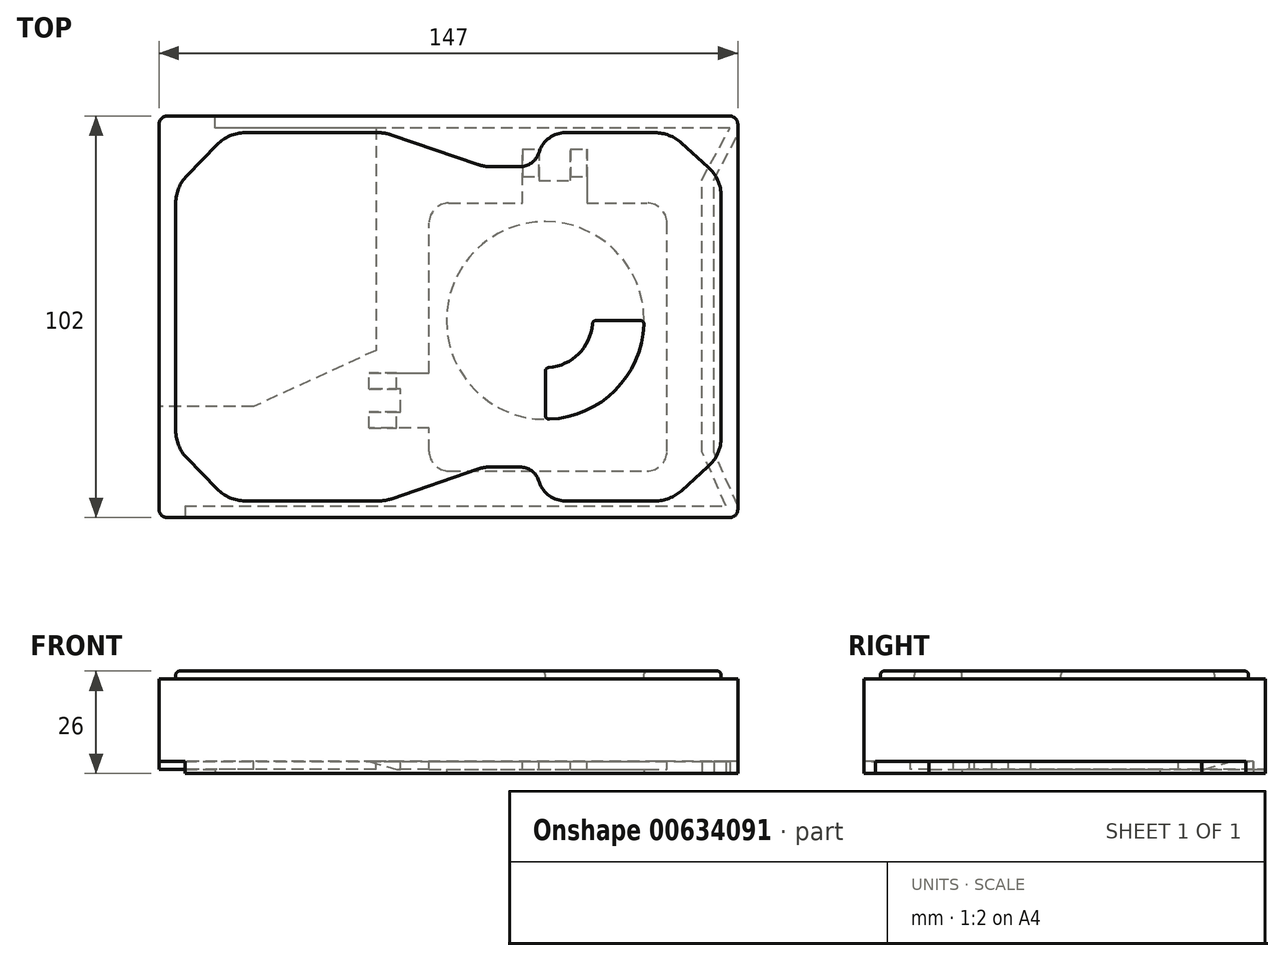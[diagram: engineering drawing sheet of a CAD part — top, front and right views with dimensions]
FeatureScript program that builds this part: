
annotation { "Feature Type Name" : "Feature", "Feature Type Description" : "" }
export const myFeature = defineFeature(function(context is Context, id is Id, definition is map)
    precondition{}
    {
        {
            var Q0;
            Q0=qCreatedBy(makeId("Top.planeOp"),FACE);
            var sketch = newSketch(context, id + "F0", { "sketchPlane" : qUnion([Q0])});
            skLineSegment(sketch, "E0.bottom", {"start": v(0, 0) * mm, "end": v(147, 0) * mm});
            skLineSegment(sketch, "E0.top", {"start": v(0, 102) * mm, "end": v(147, 102) * mm});
            skLineSegment(sketch, "E0.left", {"start": v(0, 0) * mm, "end": v(0, 102) * mm});
            skLineSegment(sketch, "E0.right", {"start": v(147, 0) * mm, "end": v(147, 102) * mm});
            skSolve(sketch);
        }
        {
            var Q0;
            Q0=makeQuery(id+"F0.imprint","IMPRINT",FACE,{"disambiguationData":[TD([[makeQuery(id+"F0.imprint","IMPRINT",EDGE,{"derivedFrom":sQuery(id+"F0.wireOp",EDGE,"E0.bottom")}),1.0]])]});
            extrude(context, id + "F1", {"entities" : qUnion([Q0]), "depth" : 26 * mm, "offsetDistance" : 25 * mm});
        }
        {
            var Q0;
            Q0=makeQuery(id+"F1.opExtrude","SWEPT_EDGE",EDGE,{"disambiguationData":[OSD([sQuery(id+"F0.wireOp",EDGE,"E0.bottom"),sQuery(id+"F0.wireOp",EDGE,"E0.left")])]});
            var Q1;
            Q1=makeQuery(id+"F1.opExtrude","SWEPT_EDGE",EDGE,{"disambiguationData":[OSD([sQuery(id+"F0.wireOp",EDGE,"E0.bottom"),sQuery(id+"F0.wireOp",EDGE,"E0.right")])]});
            var Q2;
            Q2=makeQuery(id+"F1.opExtrude","SWEPT_EDGE",EDGE,{"disambiguationData":[OSD([sQuery(id+"F0.wireOp",EDGE,"E0.top"),sQuery(id+"F0.wireOp",EDGE,"E0.right")])]});
            var Q3;
            Q3=makeQuery(id+"F1.opExtrude","SWEPT_EDGE",EDGE,{"disambiguationData":[OSD([sQuery(id+"F0.wireOp",EDGE,"E0.top"),sQuery(id+"F0.wireOp",EDGE,"E0.left")])]});
            fillet(context, id + "F2", {"entities" : qUnion([Q0, Q1, Q2, Q3]), "radius" : 2 * mm, "tangentPropagation" : true, "allowEdgeOverflow" : false});
        }
        {
            var Q0;
            Q0=makeQuery(id+"F1.opExtrude","CAP_FACE",FACE,{"disambiguationData":[OSD([sQuery(id+"F0.wireOp",EDGE,"E0.bottom"),sQuery(id+"F0.wireOp",EDGE,"E0.top"),sQuery(id+"F0.wireOp",EDGE,"E0.left"),sQuery(id+"F0.wireOp",EDGE,"E0.right")])],"isStart":true});
            var sketch = newSketch(context, id + "F3", { "sketchPlane" : qUnion([Q0])});
            skLineSegment(sketch, "E1", {"start": v(6.56, -3) * mm, "end": v(144, -3) * mm});
            skLineSegment(sketch, "E2", {"start": v(144, -3) * mm, "end": v(137.95, -16.63) * mm});
            skLineSegment(sketch, "E3", {"start": v(137.95, -16.63) * mm, "end": v(137.95, -85.86) * mm});
            skLineSegment(sketch, "E4", {"start": v(137.95, -85.86) * mm, "end": v(145, -99) * mm});
            skLineSegment(sketch, "E5", {"start": v(145, -99) * mm, "end": v(14.23, -99) * mm});
            skLineSegment(sketch, "E6", {"start": v(6.56, -3) * mm, "end": v(6.56, 0) * mm});
            skLineSegment(sketch, "E7", {"start": v(147, -3) * mm, "end": v(140.95, -16.63) * mm});
            skLineSegment(sketch, "E8", {"start": v(140.95, -16.63) * mm, "end": v(140.95, -85.86) * mm});
            skLineSegment(sketch, "E9", {"start": v(140.95, -85.86) * mm, "end": v(147, -97.14) * mm});
            skLineSegment(sketch, "E10", {"start": v(14.23, -99) * mm, "end": v(14.23, -102) * mm});
            skLineSegment(sketch, "E11", {"start": v(140.95, -16.63) * mm, "end": v(137.95, -16.63) * mm, "construction": true});
            skLineSegment(sketch, "E12", {"start": v(145, -99) * mm, "end": v(147, -99) * mm, "construction": true});
            skLineSegment(sketch, "E13", {"start": v(144, -3) * mm, "end": v(147, -3) * mm, "construction": true});
            skLineSegment(sketch, "E14", {"start": v(137.95, -85.86) * mm, "end": v(140.95, -85.86) * mm, "construction": true});
            skCircle(sketch, "E15", {"center": v(98.1, -50.09) * mm, "radius": 25.12 * mm});
            skSolve(sketch);
        }
        {
            var Q0;
            Q0=makeQuery(id+"F3.imprint","IMPRINT",FACE,{"disambiguationData":[TD([[makeQuery(id+"F3.imprint","IMPRINT",EDGE,{"derivedFrom":sQuery(id+"F3.wireOp",EDGE,"E1")}),-1.0]])]});
            var Q1;
            Q1=makeQuery(id+"F3.imprint","IMPRINT",FACE,{"disambiguationData":[TD([[makeQuery(id+"F3.imprint","IMPRINT",EDGE,{"derivedFrom":sQuery(id+"F3.wireOp",EDGE,"E7")}),1.0]])]});
            extrude(context, id + "F4", {"entities" : qUnion([Q0, Q1]), "operationType" : NewBodyOperationType.REMOVE, "oppositeDirection" : true, "depth" : 3 * mm, "offsetDistance" : 25 * mm});
        }
        {
            var Q0;
            Q0=makeQuery(id+"F4.boolean.opBoolean","COPY",FACE,{"derivedFrom":makeQuery(id+"F4.opExtrude","CAP_FACE",FACE,{"disambiguationData":[OSD([sQuery(id+"F0.wireOp",EDGE,"E0.bottom"),sQuery(id+"F0.wireOp",EDGE,"E0.top"),sQuery(id+"F0.wireOp",EDGE,"E0.left"),sQuery(id+"F0.wireOp",EDGE,"E0.right"),sQuery(id+"F3.wireOp",EDGE,"E1"),sQuery(id+"F3.wireOp",EDGE,"E2"),sQuery(id+"F3.wireOp",EDGE,"E3"),sQuery(id+"F3.wireOp",EDGE,"E4"),sQuery(id+"F3.wireOp",EDGE,"E5"),sQuery(id+"F3.wireOp",EDGE,"E6"),sQuery(id+"F3.wireOp",EDGE,"E10"),sQuery(id+"F3.wireOp",EDGE,"E15")])],"isStart":false})});
            var sketch = newSketch(context, id + "F5", { "sketchPlane" : qUnion([Q0])});
            skLineSegment(sketch, "E16", {"start": v(55.07, -99) * mm, "end": v(55.07, -42.5) * mm});
            skLineSegment(sketch, "E17", {"start": v(55.07, -42.5) * mm, "end": v(23.96, -28.17) * mm});
            skLineSegment(sketch, "E18", {"start": v(23.96, -28.17) * mm, "end": v(0, -28.17) * mm});
            skSolve(sketch);
        }
        {
            var Q0;
            {var subQ3=sQuery(id+"F5.wireOp",EDGE,"E16");Q0=makeQuery(id+"F5.imprint","IMPRINT",FACE,{"disambiguationData":[TD([[makeQuery(id+"F5.imprint","IMPRINT",EDGE,{"derivedFrom":subQ3}),1.0]])]});}
            extrude(context, id + "F6", {"entities" : qUnion([Q0]), "operationType" : NewBodyOperationType.ADD, "depth" : 2 * mm, "offsetDistance" : 25 * mm});
        }
        {
            var Q0;
            Q0=makeQuery(id+"F4.boolean.opBoolean","COPY",FACE,{"derivedFrom":makeQuery(id+"F4.opExtrude","CAP_FACE",FACE,{"disambiguationData":[OSD([sQuery(id+"F0.wireOp",EDGE,"E0.bottom"),sQuery(id+"F0.wireOp",EDGE,"E0.top"),sQuery(id+"F0.wireOp",EDGE,"E0.left"),sQuery(id+"F0.wireOp",EDGE,"E0.right"),sQuery(id+"F3.wireOp",EDGE,"E1"),sQuery(id+"F3.wireOp",EDGE,"E2"),sQuery(id+"F3.wireOp",EDGE,"E3"),sQuery(id+"F3.wireOp",EDGE,"E4"),sQuery(id+"F3.wireOp",EDGE,"E5"),sQuery(id+"F3.wireOp",EDGE,"E6"),sQuery(id+"F3.wireOp",EDGE,"E10"),sQuery(id+"F3.wireOp",EDGE,"E15")])],"isStart":false})});
            var sketch = newSketch(context, id + "F7", { "sketchPlane" : qUnion([Q0])});
            skLineSegment(sketch, "E19", {"start": v(68.58, -22.73) * mm, "end": v(53.34, -22.73) * mm});
            skLineSegment(sketch, "E20", {"start": v(53.34, -22.73) * mm, "end": v(53.34, -26.85) * mm});
            skLineSegment(sketch, "E21", {"start": v(53.34, -26.85) * mm, "end": v(61.31, -26.85) * mm});
            skLineSegment(sketch, "E22", {"start": v(61.31, -26.85) * mm, "end": v(61.31, -32.61) * mm});
            skLineSegment(sketch, "E23", {"start": v(61.31, -32.61) * mm, "end": v(53.34, -32.61) * mm});
            skLineSegment(sketch, "E24", {"start": v(53.34, -32.61) * mm, "end": v(53.34, -36.74) * mm});
            skLineSegment(sketch, "E25", {"start": v(53.34, -36.74) * mm, "end": v(68.58, -36.74) * mm});
            skLineSegment(sketch, "E26", {"start": v(92.32, -79.88) * mm, "end": v(92.32, -93.65) * mm});
            skLineSegment(sketch, "E27", {"start": v(92.32, -93.65) * mm, "end": v(96.45, -93.65) * mm});
            skLineSegment(sketch, "E28", {"start": v(96.45, -93.65) * mm, "end": v(96.45, -85.67) * mm});
            skLineSegment(sketch, "E29", {"start": v(96.45, -85.67) * mm, "end": v(104.52, -85.67) * mm});
            skLineSegment(sketch, "E30", {"start": v(104.52, -85.67) * mm, "end": v(104.52, -93.65) * mm});
            skLineSegment(sketch, "E31", {"start": v(104.52, -93.65) * mm, "end": v(108.64, -93.65) * mm});
            skLineSegment(sketch, "E32", {"start": v(108.64, -93.65) * mm, "end": v(108.64, -79.88) * mm});
            skLineSegment(sketch, "E33.bottom", {"start": v(68.58, -11.84) * mm, "end": v(129, -11.84) * mm});
            skLineSegment(sketch, "E33.top", {"start": v(68.58, -79.88) * mm, "end": v(129, -79.88) * mm});
            skLineSegment(sketch, "E33.left", {"start": v(68.58, -11.84) * mm, "end": v(68.58, -79.88) * mm});
            skLineSegment(sketch, "E33.right", {"start": v(129, -11.84) * mm, "end": v(129, -79.88) * mm});
            skLineSegment(sketch, "E34", {"start": v(61.31, -26.85) * mm, "end": v(61.31, -22.73) * mm});
            skLineSegment(sketch, "E35", {"start": v(61.31, -32.61) * mm, "end": v(61.31, -36.74) * mm});
            skLineSegment(sketch, "E36", {"start": v(96.45, -85.67) * mm, "end": v(92.32, -85.67) * mm});
            skLineSegment(sketch, "E37", {"start": v(104.52, -85.67) * mm, "end": v(108.64, -85.67) * mm});
            skSolve(sketch);
        }
        {
            var Q0;
            {var subQ6=sQuery(id+"F7.wireOp",EDGE,"E33.bottom");Q0=makeQuery(id+"F7.imprint","IMPRINT",FACE,{"disambiguationData":[TD([[makeQuery(id+"F7.imprint","IMPRINT",EDGE,{"derivedFrom":subQ6}),-1.0]])]});}
            var Q1;
            Q1=makeQuery(id+"F7.imprint","IMPRINT",FACE,{"disambiguationData":[TD([[makeQuery(id+"F7.imprint","IMPRINT",EDGE,{"derivedFrom":sQuery(id+"F7.wireOp",EDGE,"E22")}),1.0]])]});
            var Q2;
            Q2=makeQuery(id+"F7.imprint","IMPRINT",FACE,{"disambiguationData":[TD([[makeQuery(id+"F7.imprint","IMPRINT",EDGE,{"derivedFrom":sQuery(id+"F7.wireOp",EDGE,"E29")}),1.0]])]});
            var Q3;
            {var subQ0=sQuery(id+"F7.wireOp",EDGE,"E20");Q3=makeQuery(id+"F7.imprint","IMPRINT",FACE,{"disambiguationData":[TD([[makeQuery(id+"F7.imprint","IMPRINT",EDGE,{"derivedFrom":subQ0}),1.0]])]});}
            var Q4;
            Q4=makeQuery(id+"F7.imprint","IMPRINT",FACE,{"disambiguationData":[TD([[makeQuery(id+"F7.imprint","IMPRINT",EDGE,{"derivedFrom":sQuery(id+"F7.wireOp",EDGE,"E23")}),1.0]])]});
            var Q5;
            {var subQ0=sQuery(id+"F7.wireOp",EDGE,"E27");Q5=makeQuery(id+"F7.imprint","IMPRINT",FACE,{"disambiguationData":[TD([[makeQuery(id+"F7.imprint","IMPRINT",EDGE,{"derivedFrom":subQ0}),1.0]])]});}
            var Q6;
            Q6=makeQuery(id+"F7.imprint","IMPRINT",FACE,{"disambiguationData":[TD([[makeQuery(id+"F7.imprint","IMPRINT",EDGE,{"derivedFrom":sQuery(id+"F7.wireOp",EDGE,"E30")}),1.0]])]});
            extrude(context, id + "F8", {"entities" : qUnion([Q0, Q1, Q2, Q3, Q4, Q5, Q6]), "operationType" : NewBodyOperationType.ADD, "depth" : 2 * mm, "offsetDistance" : 25 * mm});
        }
        {
            var Q0;
            Q0=makeQuery(id+"F8.opExtrude","CAP_EDGE",EDGE,{"disambiguationData":[OSD([sQuery(id+"F7.wireOp",EDGE,"E20")])],"isStart":false});
            var Q1;
            Q1=makeQuery(id+"F8.opExtrude","CAP_EDGE",EDGE,{"disambiguationData":[OSD([sQuery(id+"F7.wireOp",EDGE,"E24")])],"isStart":false});
            var Q2;
            Q2=makeQuery(id+"F8.opExtrude","CAP_EDGE",EDGE,{"disambiguationData":[OSD([sQuery(id+"F7.wireOp",EDGE,"E27")])],"isStart":false});
            var Q3;
            Q3=makeQuery(id+"F8.opExtrude","CAP_EDGE",EDGE,{"disambiguationData":[OSD([sQuery(id+"F7.wireOp",EDGE,"E31")])],"isStart":false});
            chamfer(context, id + "F9", {"entities" : qUnion([Q0, Q1, Q2, Q3]), "chamferType" : ChamferType.TWO_OFFSETS, "width1" : 7 * mm, "oppositeDirection" : false, "width2" : 2 * mm, "tangentPropagation" : true});
        }
        {
            var Q0;
            Q0=makeQuery(id+"F8.opExtrude","SWEPT_EDGE",EDGE,{"disambiguationData":[OSD([sQuery(id+"F7.wireOp",EDGE,"E33.bottom"),sQuery(id+"F7.wireOp",EDGE,"E33.left")])]});
            var Q1;
            Q1=makeQuery(id+"F8.opExtrude","SWEPT_EDGE",EDGE,{"disambiguationData":[OSD([sQuery(id+"F7.wireOp",EDGE,"E33.bottom"),sQuery(id+"F7.wireOp",EDGE,"E33.right")])]});
            var Q2;
            Q2=makeQuery(id+"F8.opExtrude","SWEPT_EDGE",EDGE,{"disambiguationData":[OSD([sQuery(id+"F7.wireOp",EDGE,"E33.top"),sQuery(id+"F7.wireOp",EDGE,"E33.right")])]});
            var Q3;
            Q3=makeQuery(id+"F8.opExtrude","SWEPT_EDGE",EDGE,{"disambiguationData":[OSD([sQuery(id+"F7.wireOp",EDGE,"E33.top"),sQuery(id+"F7.wireOp",EDGE,"E33.left")])]});
            fillet(context, id + "F10", {"entities" : qUnion([Q0, Q1, Q2, Q3]), "radius" : 5 * mm, "tangentPropagation" : true, "allowEdgeOverflow" : false});
        }
        {
            var Q0;
            Q0=makeQuery(id+"F1.opExtrude","CAP_FACE",FACE,{"disambiguationData":[OSD([sQuery(id+"F0.wireOp",EDGE,"E0.bottom"),sQuery(id+"F0.wireOp",EDGE,"E0.top"),sQuery(id+"F0.wireOp",EDGE,"E0.left"),sQuery(id+"F0.wireOp",EDGE,"E0.right")])],"isStart":false});
            var sketch = newSketch(context, id + "F11", { "sketchPlane" : qUnion([Q0])});
            skLineSegment(sketch, "E38", {"start": v(4.23, 51) * mm, "end": v(4.23, 22.07) * mm});
            skLineSegment(sketch, "E39", {"start": v(7.06, 15.1) * mm, "end": v(14.7, 7.25) * mm});
            skLineSegment(sketch, "E40", {"start": v(21.86, 4.23) * mm, "end": v(55.75, 4.23) * mm});
            skLineSegment(sketch, "E41", {"start": v(59, 4.77) * mm, "end": v(80.96, 12.3) * mm});
            skLineSegment(sketch, "E42", {"start": v(84.2, 12.84) * mm, "end": v(91.68, 12.84) * mm});
            skLineSegment(sketch, "E43", {"start": v(96.41, 9.47) * mm, "end": v(96.59, 8.95) * mm});
            skLineSegment(sketch, "E44", {"start": v(103.21, 4.23) * mm, "end": v(125.96, 4.23) * mm});
            skLineSegment(sketch, "E45", {"start": v(132.66, 6.8) * mm, "end": v(139.47, 12.94) * mm});
            skLineSegment(sketch, "E46", {"start": v(142.77, 20.37) * mm, "end": v(142.77, 51) * mm});
            skLineSegment(sketch, "E47", {"start": v(147, 51) * mm, "end": v(0, 51) * mm, "construction": true});
            skLineSegment(sketch, "E48", {"start": v(4.23, 51) * mm, "end": v(0, 51) * mm, "construction": true});
            skLineSegment(sketch, "E49", {"start": v(142.77, 51) * mm, "end": v(147, 51) * mm, "construction": true});
            skLineSegment(sketch, "E50", {"start": v(129.8, 4.23) * mm, "end": v(129.8, 0) * mm, "construction": true});
            skPoint(sketch, "E51.visualSharp", {"position": v(142.77, 15.92) * mm});
            skArc(sketch, "E51.filletArc", {"start": v(139.47, 12.94) * mm, "mid": v(141.91, 16.3) * mm, "end": v(142.77, 20.37) * mm});
            skPoint(sketch, "E52.visualSharp", {"position": v(129.8, 4.23) * mm});
            skArc(sketch, "E52.filletArc", {"start": v(125.96, 4.23) * mm, "mid": v(129.55, 4.9) * mm, "end": v(132.66, 6.8) * mm});
            skPoint(sketch, "E53.visualSharp", {"position": v(98.21, 4.23) * mm});
            skArc(sketch, "E53.filletArc", {"start": v(96.59, 8.95) * mm, "mid": v(99.14, 5.53) * mm, "end": v(103.21, 4.23) * mm});
            skPoint(sketch, "E54.visualSharp", {"position": v(82.54, 12.84) * mm});
            skArc(sketch, "E54.filletArc", {"start": v(84.2, 12.84) * mm, "mid": v(82.56, 12.7) * mm, "end": v(80.96, 12.3) * mm});
            skPoint(sketch, "E55.visualSharp", {"position": v(57.42, 4.23) * mm});
            skArc(sketch, "E55.filletArc", {"start": v(55.75, 4.23) * mm, "mid": v(57.4, 4.36) * mm, "end": v(59, 4.77) * mm});
            skPoint(sketch, "E56.visualSharp", {"position": v(17.64, 4.23) * mm});
            skArc(sketch, "E56.filletArc", {"start": v(14.7, 7.25) * mm, "mid": v(17.97, 5.01) * mm, "end": v(21.86, 4.23) * mm});
            skPoint(sketch, "E57.visualSharp", {"position": v(4.23, 18) * mm});
            skArc(sketch, "E57.filletArc", {"start": v(4.23, 22.07) * mm, "mid": v(4.96, 18.3) * mm, "end": v(7.06, 15.1) * mm});
            skPoint(sketch, "E58.visualSharp", {"position": v(95.25, 12.84) * mm});
            skArc(sketch, "E58.filletArc", {"start": v(96.41, 9.47) * mm, "mid": v(94.59, 11.91) * mm, "end": v(91.68, 12.84) * mm});
            skLineSegment(sketch, "E59.MirrorCS", {"start": v(96.41, 92.53) * mm, "end": v(96.59, 93.05) * mm});
            skArc(sketch, "E60.MirrorCS", {"start": v(125.96, 97.77) * mm, "mid": v(129.55, 97.1) * mm, "end": v(132.66, 95.2) * mm});
            skArc(sketch, "E61.MirrorCS", {"start": v(84.2, 89.16) * mm, "mid": v(82.56, 89.3) * mm, "end": v(80.96, 89.7) * mm});
            skArc(sketch, "E62.MirrorCS", {"start": v(55.75, 97.77) * mm, "mid": v(57.4, 97.64) * mm, "end": v(59, 97.23) * mm});
            skArc(sketch, "E63.MirrorCS", {"start": v(14.7, 94.75) * mm, "mid": v(17.97, 96.99) * mm, "end": v(21.86, 97.77) * mm});
            skArc(sketch, "E64.MirrorCS", {"start": v(96.41, 92.53) * mm, "mid": v(94.59, 90.09) * mm, "end": v(91.68, 89.16) * mm});
            skArc(sketch, "E65.MirrorCS", {"start": v(4.23, 79.93) * mm, "mid": v(4.96, 83.7) * mm, "end": v(7.06, 86.9) * mm});
            skArc(sketch, "E66.MirrorCS", {"start": v(96.59, 93.05) * mm, "mid": v(99.14, 96.47) * mm, "end": v(103.21, 97.77) * mm});
            skArc(sketch, "E67.MirrorCS", {"start": v(139.47, 89.06) * mm, "mid": v(141.91, 85.7) * mm, "end": v(142.77, 81.63) * mm});
            skPoint(sketch, "E68.MirrorP", {"position": v(4.23, 84) * mm});
            skPoint(sketch, "E69.MirrorP", {"position": v(129.8, 97.77) * mm});
            skLineSegment(sketch, "E70.MirrorCS", {"start": v(4.23, 51) * mm, "end": v(4.23, 79.93) * mm});
            skLineSegment(sketch, "E71.MirrorCS", {"start": v(103.21, 97.77) * mm, "end": v(125.96, 97.77) * mm});
            skPoint(sketch, "E72.MirrorP", {"position": v(98.21, 97.77) * mm});
            skLineSegment(sketch, "E73.MirrorCS", {"start": v(132.66, 95.2) * mm, "end": v(139.47, 89.06) * mm});
            skLineSegment(sketch, "E74.MirrorCS", {"start": v(21.86, 97.77) * mm, "end": v(55.75, 97.77) * mm});
            skPoint(sketch, "E75.MirrorP", {"position": v(17.64, 97.77) * mm});
            skLineSegment(sketch, "E76.MirrorCS", {"start": v(7.06, 86.9) * mm, "end": v(14.7, 94.75) * mm});
            skLineSegment(sketch, "E77.MirrorCS", {"start": v(59, 97.23) * mm, "end": v(80.96, 89.7) * mm});
            skPoint(sketch, "E78.MirrorP", {"position": v(82.54, 89.16) * mm});
            skPoint(sketch, "E79.MirrorP", {"position": v(142.77, 86.08) * mm});
            skPoint(sketch, "E80.MirrorP", {"position": v(95.25, 89.16) * mm});
            skPoint(sketch, "E81.MirrorP", {"position": v(57.42, 97.77) * mm});
            skLineSegment(sketch, "E82.MirrorCS", {"start": v(84.2, 89.16) * mm, "end": v(91.68, 89.16) * mm});
            skLineSegment(sketch, "E83.MirrorCS", {"start": v(142.77, 81.63) * mm, "end": v(142.77, 51) * mm});
            skLineSegment(sketch, "E84", {"start": v(98.1, 37.13) * mm, "end": v(98.1, 26) * mm});
            skLineSegment(sketch, "E85", {"start": v(122.2, 50.09) * mm, "end": v(111.06, 50.09) * mm});
            skLineSegment(sketch, "E86", {"start": v(110.1, 50.09) * mm, "end": v(98.1, 50.09) * mm, "construction": true});
            skLineSegment(sketch, "E87", {"start": v(98.1, 50.09) * mm, "end": v(98.1, 38.09) * mm, "construction": true});
            skArc(sketch, "E88", {"start": v(99.02, 38.12) * mm, "mid": v(106.58, 41.6) * mm, "end": v(110.06, 49.16) * mm});
            skArc(sketch, "E89", {"start": v(99.14, 25) * mm, "mid": v(115.86, 32.33) * mm, "end": v(123.2, 49.05) * mm});
            skPoint(sketch, "E90.visualSharp", {"position": v(123.22, 50.09) * mm});
            skArc(sketch, "E90.filletArc", {"start": v(123.2, 49.05) * mm, "mid": v(122.92, 49.78) * mm, "end": v(122.2, 50.09) * mm});
            skPoint(sketch, "E91.visualSharp", {"position": v(98.1, 24.97) * mm});
            skArc(sketch, "E91.filletArc", {"start": v(98.1, 26) * mm, "mid": v(98.4, 25.27) * mm, "end": v(99.14, 25) * mm});
            skPoint(sketch, "E92.visualSharp", {"position": v(98.1, 38.09) * mm});
            skArc(sketch, "E92.filletArc", {"start": v(99.02, 38.12) * mm, "mid": v(98.37, 37.8) * mm, "end": v(98.1, 37.13) * mm});
            skPoint(sketch, "E93.visualSharp", {"position": v(110.1, 50.09) * mm});
            skArc(sketch, "E93.filletArc", {"start": v(111.06, 50.09) * mm, "mid": v(110.38, 49.82) * mm, "end": v(110.06, 49.16) * mm});
            skCircle(sketch, "E94.0", {"center": v(98.1, 50.09) * mm, "radius": 25.12 * mm, "construction": true});
            skSolve(sketch);
        }
        {
            var Q0;
            Q0=makeQuery(id+"F11.imprint","IMPRINT",FACE,{"disambiguationData":[TD([[makeQuery(id+"F11.imprint","IMPRINT",EDGE,{"derivedFrom":sQuery(id+"F11.wireOp",EDGE,"E38")}),-1.0]])]});
            var Q1;
            Q1=makeQuery(id+"F11.imprint","IMPRINT",FACE,{"disambiguationData":[TD([[makeQuery(id+"F11.imprint","IMPRINT",EDGE,{"derivedFrom":sQuery(id+"F11.wireOp",EDGE,"E84")}),1.0]])]});
            extrude(context, id + "F12", {"entities" : qUnion([Q0, Q1]), "operationType" : NewBodyOperationType.REMOVE, "oppositeDirection" : true, "depth" : 2 * mm, "offsetDistance" : 25 * mm});
        }
        {
            var Q0;
            Q0=makeQuery(id+"F1.opExtrude","CAP_FACE",FACE,{"disambiguationData":[OSD([sQuery(id+"F0.wireOp",EDGE,"E0.bottom"),sQuery(id+"F0.wireOp",EDGE,"E0.top"),sQuery(id+"F0.wireOp",EDGE,"E0.left"),sQuery(id+"F0.wireOp",EDGE,"E0.right")])],"isStart":false});
            fillet(context, id + "F13", {"entities" : qUnion([Q0]), "radius" : 1 * mm, "tangentPropagation" : true, "allowEdgeOverflow" : false});
        }
    });
